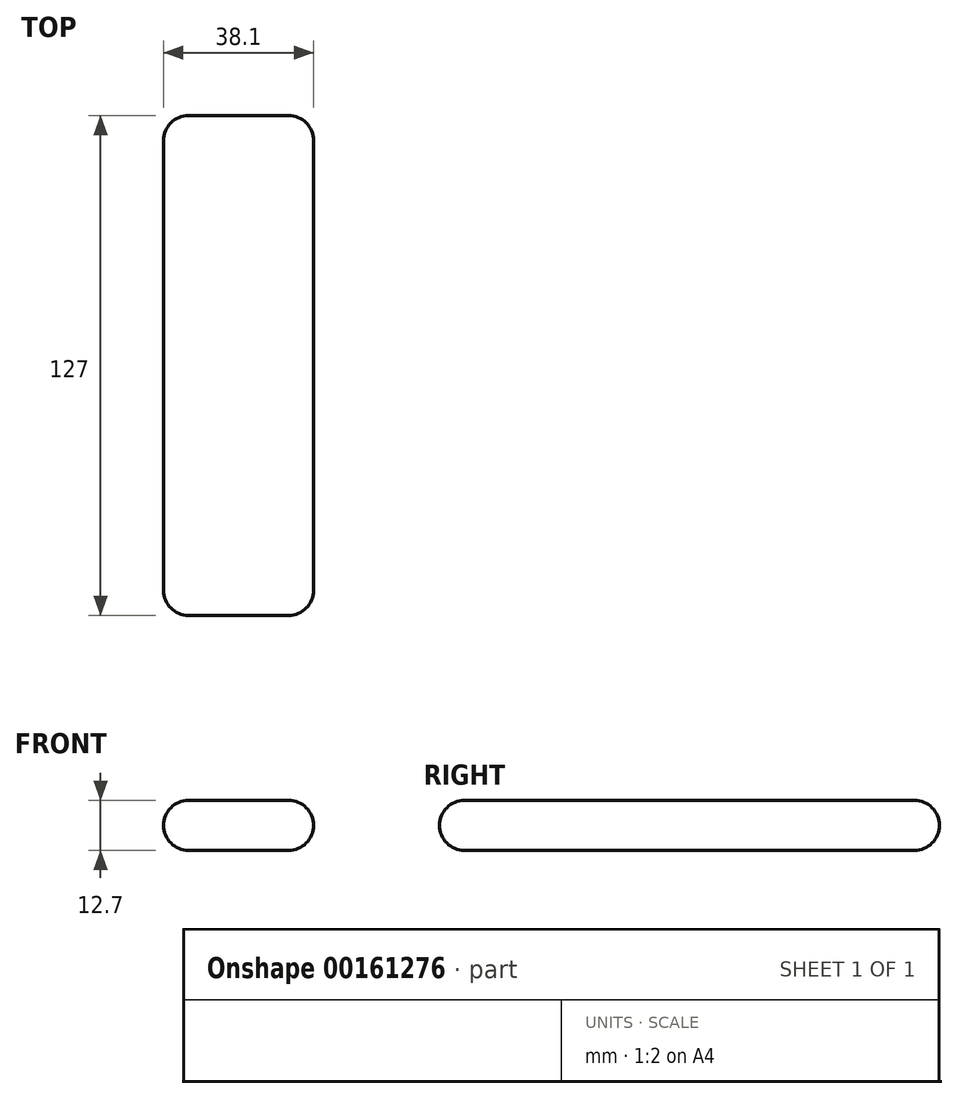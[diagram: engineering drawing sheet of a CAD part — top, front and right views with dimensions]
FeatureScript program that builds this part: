
annotation { "Feature Type Name" : "Feature", "Feature Type Description" : "" }
export const myFeature = defineFeature(function(context is Context, id is Id, definition is map)
    precondition{}
    {
        {
            var Q0;
            Q0=qCreatedBy(makeId("Top.planeOp"),FACE);
            var sketch = newSketch(context, id + "F0", { "sketchPlane" : qUnion([Q0])});
            skLineSegment(sketch, "E0.bottom", {"start": v(19.05, 63.5) * mm, "end": v(-19.05, 63.5) * mm});
            skLineSegment(sketch, "E0.top", {"start": v(19.05, -63.5) * mm, "end": v(-19.05, -63.5) * mm});
            skLineSegment(sketch, "E0.left", {"start": v(19.05, 63.5) * mm, "end": v(19.05, -63.5) * mm});
            skLineSegment(sketch, "E0.right", {"start": v(-19.05, 63.5) * mm, "end": v(-19.05, -63.5) * mm});
            skPoint(sketch, "E0.middle", {"position": v(0, 0) * mm});
            skSolve(sketch);
        }
        {
            var Q0;
            Q0=makeQuery(id+"F0.imprint","IMPRINT",FACE,{"disambiguationData":[TD([[makeQuery(id+"F0.imprint","IMPRINT",EDGE,{"derivedFrom":sQuery(id+"F0.wireOp",EDGE,"E0.bottom")}),1.0]])]});
            extrude(context, id + "F1", {"entities" : qUnion([Q0]), "depth" : 12.7 * mm});
        }
        {
            var Q0;
            Q0=makeQuery(id+"F1.opExtrude","CAP_EDGE",EDGE,{"disambiguationData":[OSD([sQuery(id+"F0.wireOp",EDGE,"E0.right")])],"isStart":false});
            var Q1;
            Q1=makeQuery(id+"F1.opExtrude","CAP_EDGE",EDGE,{"disambiguationData":[OSD([sQuery(id+"F0.wireOp",EDGE,"E0.right")])],"isStart":true});
            var Q2;
            Q2=makeQuery(id+"F1.opExtrude","CAP_EDGE",EDGE,{"disambiguationData":[OSD([sQuery(id+"F0.wireOp",EDGE,"E0.left")])],"isStart":true});
            var Q3;
            Q3=makeQuery(id+"F1.opExtrude","CAP_EDGE",EDGE,{"disambiguationData":[OSD([sQuery(id+"F0.wireOp",EDGE,"E0.left")])],"isStart":false});
            var Q4;
            Q4=makeQuery(id+"F1.opExtrude","CAP_EDGE",EDGE,{"disambiguationData":[OSD([sQuery(id+"F0.wireOp",EDGE,"E0.top")])],"isStart":true});
            var Q5;
            Q5=makeQuery(id+"F1.opExtrude","SWEPT_EDGE",EDGE,{"disambiguationData":[OSD([sQuery(id+"F0.wireOp",EDGE,"E0.top"),sQuery(id+"F0.wireOp",EDGE,"E0.right")])]});
            var Q6;
            Q6=makeQuery(id+"F1.opExtrude","SWEPT_EDGE",EDGE,{"disambiguationData":[OSD([sQuery(id+"F0.wireOp",EDGE,"E0.top"),sQuery(id+"F0.wireOp",EDGE,"E0.left")])]});
            var Q7;
            Q7=makeQuery(id+"F1.opExtrude","CAP_EDGE",EDGE,{"disambiguationData":[OSD([sQuery(id+"F0.wireOp",EDGE,"E0.top")])],"isStart":false});
            var Q8;
            Q8=makeQuery(id+"F1.opExtrude","SWEPT_FACE",FACE,{"disambiguationData":[OSD([sQuery(id+"F0.wireOp",EDGE,"E0.bottom")])]});
            var Q9;
            Q9=makeQuery(id+"F1.opExtrude","CAP_EDGE",EDGE,{"disambiguationData":[OSD([sQuery(id+"F0.wireOp",EDGE,"E0.bottom")])],"isStart":false});
            var Q10;
            Q10=makeQuery(id+"F1.opExtrude","SWEPT_EDGE",EDGE,{"disambiguationData":[OSD([sQuery(id+"F0.wireOp",EDGE,"E0.bottom"),sQuery(id+"F0.wireOp",EDGE,"E0.left")])]});
            var Q11;
            Q11=makeQuery(id+"F1.opExtrude","SWEPT_EDGE",EDGE,{"disambiguationData":[OSD([sQuery(id+"F0.wireOp",EDGE,"E0.bottom"),sQuery(id+"F0.wireOp",EDGE,"E0.right")])]});
            fillet(context, id + "F2", {"entities" : qUnion([Q0, Q1, Q2, Q3, Q4, Q5, Q6, Q7, Q8, Q9, Q10, Q11]), "radius" : 6.35 * mm, "tangentPropagation" : true, "allowEdgeOverflow" : false});
        }
    });
